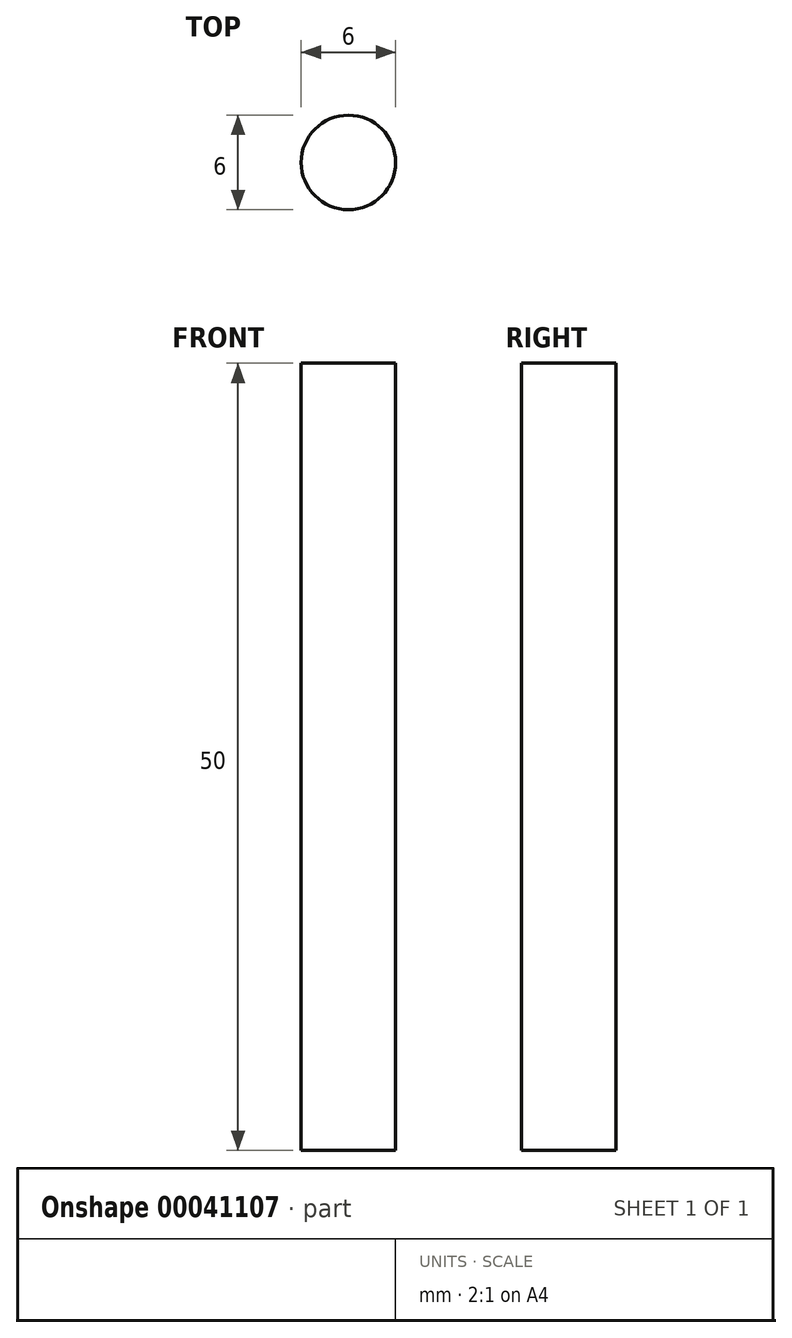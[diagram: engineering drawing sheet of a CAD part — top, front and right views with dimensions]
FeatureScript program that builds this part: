
annotation { "Feature Type Name" : "Feature", "Feature Type Description" : "" }
export const myFeature = defineFeature(function(context is Context, id is Id, definition is map)
    precondition{}
    {
        {
            var Q0;
            Q0=qCreatedBy(makeId("Top.planeOp"),FACE);
            var sketch = newSketch(context, id + "F0", { "sketchPlane" : qUnion([Q0])});
            skCircle(sketch, "E0", {"center": v(0, 0) * mm, "radius": 3 * mm});
            skSolve(sketch);
        }
        {
            var Q0;
            Q0=makeQuery(id+"F0.imprint","IMPRINT",FACE,{"disambiguationData":[TD([[makeQuery(id+"F0.imprint","IMPRINT",EDGE,{"derivedFrom":sQuery(id+"F0.wireOp",EDGE,"E0")}),1.0]])]});
            extrude(context, id + "F1", {"entities" : qUnion([Q0]), "depth" : 50 * mm});
        }
    });
